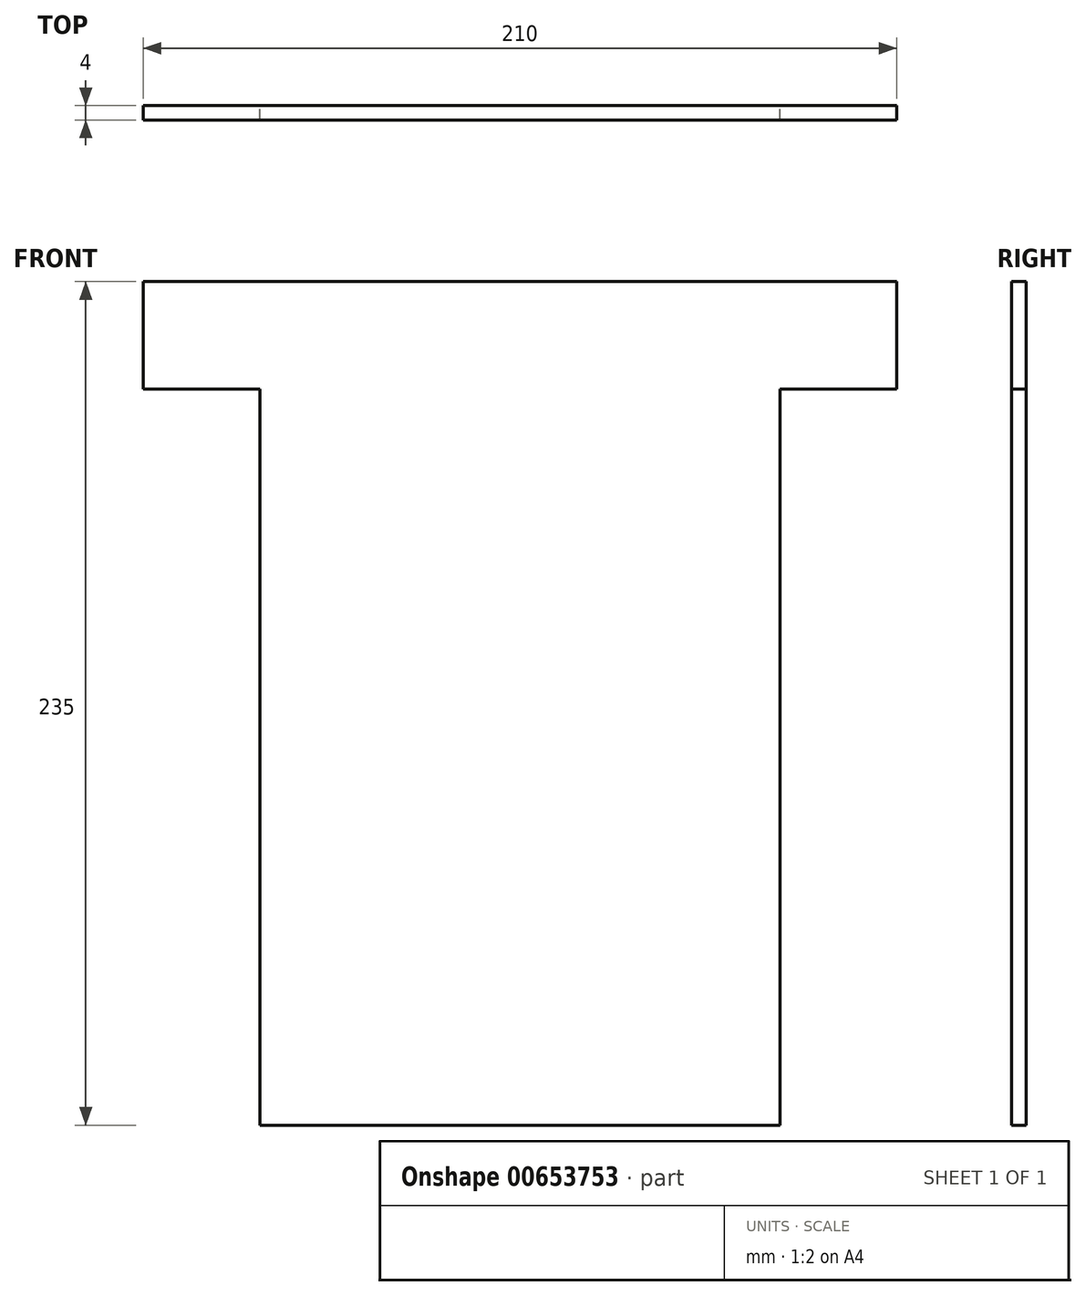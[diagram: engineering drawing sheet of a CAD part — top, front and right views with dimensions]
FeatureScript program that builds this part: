
annotation { "Feature Type Name" : "Feature", "Feature Type Description" : "" }
export const myFeature = defineFeature(function(context is Context, id is Id, definition is map)
    precondition{}
    {
        {
            var Q0;
            Q0=qCreatedBy(makeId("Front.planeOp"),FACE);
            var sketch = newSketch(context, id + "F0", { "sketchPlane" : qUnion([Q0])});
            skLineSegment(sketch, "E0", {"start": v(-132.74, 81.03) * mm, "end": v(77.26, 81.03) * mm});
            skLineSegment(sketch, "E1", {"start": v(77.26, 81.03) * mm, "end": v(77.26, 51.03) * mm});
            skLineSegment(sketch, "E2", {"start": v(77.26, 51.03) * mm, "end": v(44.76, 51.03) * mm});
            skLineSegment(sketch, "E3", {"start": v(44.76, 51.03) * mm, "end": v(44.76, -153.97) * mm});
            skLineSegment(sketch, "E4", {"start": v(44.76, -153.97) * mm, "end": v(-100.24, -153.97) * mm});
            skLineSegment(sketch, "E5", {"start": v(-100.24, -153.97) * mm, "end": v(-100.24, 51.03) * mm});
            skLineSegment(sketch, "E6", {"start": v(-100.24, 51.03) * mm, "end": v(-132.74, 51.03) * mm});
            skLineSegment(sketch, "E7", {"start": v(-132.74, 51.03) * mm, "end": v(-132.74, 81.03) * mm});
            skSolve(sketch);
        }
        {
            var Q0;
            Q0=makeQuery(id+"F0.imprint","IMPRINT",FACE,{"disambiguationData":[TD([[makeQuery(id+"F0.imprint","IMPRINT",EDGE,{"derivedFrom":sQuery(id+"F0.wireOp",EDGE,"E0")}),-1.0]])]});
            extrude(context, id + "F1", {"entities" : qUnion([Q0]), "depth" : 4 * mm, "offsetDistance" : 25 * mm});
        }
    });
